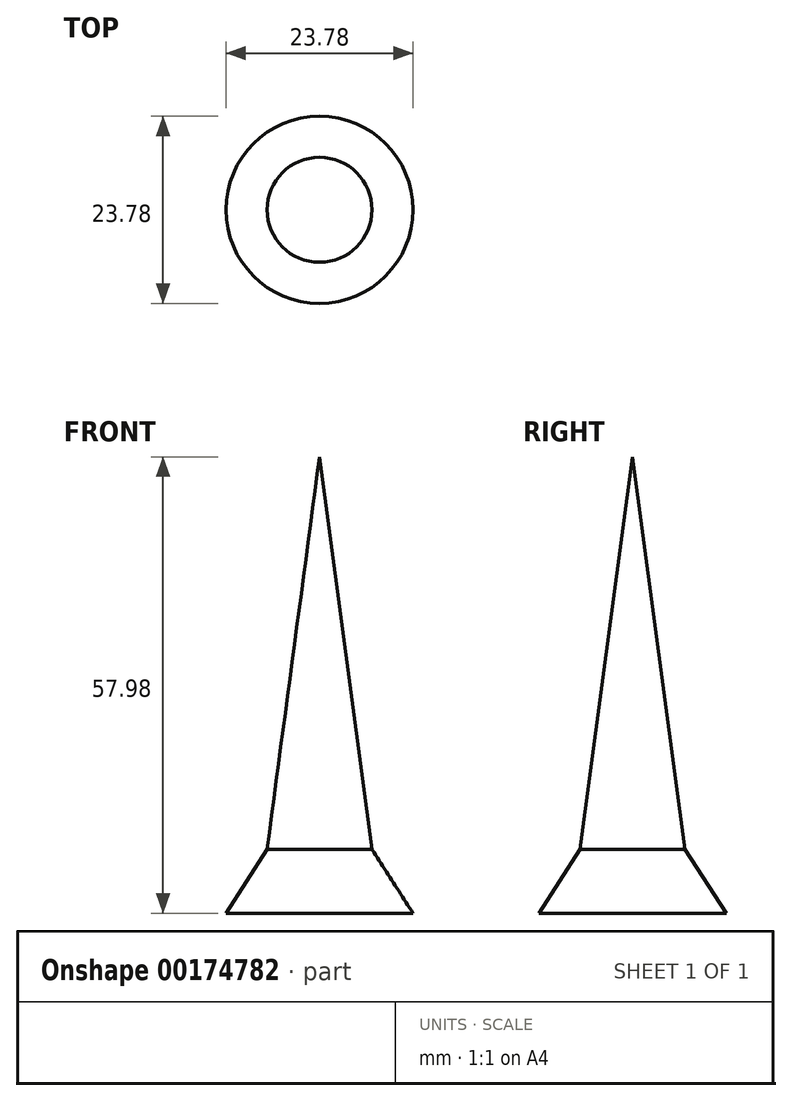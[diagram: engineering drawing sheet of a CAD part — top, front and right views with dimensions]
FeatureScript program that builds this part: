
annotation { "Feature Type Name" : "Feature", "Feature Type Description" : "" }
export const myFeature = defineFeature(function(context is Context, id is Id, definition is map)
    precondition{}
    {
        {
            var Q0;
            Q0=qCreatedBy(makeId("Front.planeOp"),FACE);
            var sketch = newSketch(context, id + "F0", { "sketchPlane" : qUnion([Q0])});
            skLineSegment(sketch, "E0", {"start": v(0, 35.08) * mm, "end": v(0, -22.9) * mm});
            skLineSegment(sketch, "E1", {"start": v(0, -22.9) * mm, "end": v(11.89, -22.9) * mm});
            skLineSegment(sketch, "E2", {"start": v(11.89, -22.9) * mm, "end": v(6.67, -14.78) * mm});
            skLineSegment(sketch, "E3", {"start": v(6.67, -14.78) * mm, "end": v(0, 35.08) * mm});
            skSolve(sketch);
        }
        {
            var Q0;
            Q0 = qSketchRegion(id + "F0", true);
            var Q1;
            Q1=sQuery(id+"F0.wireOp",EDGE,"E0");
            revolve(context, id + "F1", {"entities" : qUnion([Q0]), "axis" : qUnion([Q1]), "revolveType" : RevolveType.FULL});
        }
    });
